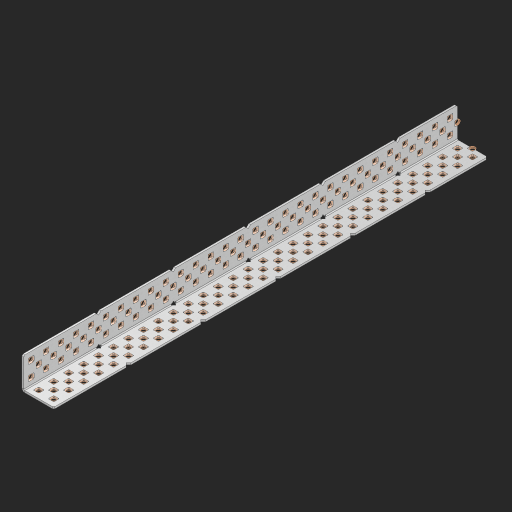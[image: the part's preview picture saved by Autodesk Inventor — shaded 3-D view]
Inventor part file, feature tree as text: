
AUTODESK INVENTOR PART (.ipt)
format: ipt  version: 2023 (Build 270158000, 158)  size: 2,022,912 bytes
history: native  units: in
note: dims shown in document units (in); Inventor stores cm internally (conversion verified against a paired STEP export)
features: other x180, extrude x172, sheet_metal_op x8, sketch x7, pattern_linear x2, mirror x1, chamfer x1
ambient origin geometry x8: Origin, YZ Plane, XZ Plane, XY Plane, X Axis, Y Axis, Z Axis, Center Point
bodies: Solid1 (feature_tree), Body (feature_tree)
feature tree (371):
  sheet_metal_op  "Flanges"
  sheet_metal_op  "Body Pattern"
  pattern_linear  "Center Pattern"  Spacing1=1.0in  [1 undecoded]
  other  "Arc Length"
  pattern_linear  "Notch Pattern"  Spacing1=0.25in  [1 undecoded]
  other  "Diagonal Plane"
  mirror  "Everything Mirrored"
  chamfer  "End Chamfer"
  sketch  "Sketch1"  dims[d0=1.0in]
  other  "Plate1"
  sketch  "Sketch2"  dims[d1=14.5in]
  other  "Plate2"
  sheet_metal_op  "Bend1"
  sheet_metal_op  "Corner1"
  sketch  "Sketch8"  dims[d2=0.0625in]
  sketch  "Sketch9"  dims[d3=0.0625in]
  other  "Srf91"
  sheet_metal_op  "Body Pattern Sketch"
  other  "Srf92"
  sketch  "Sketch13"  dims[d4=0.0312in]
  sketch  "Sketch15"  dims[d5=0.125in]
  sketch  "Sketch16"  dims[d6=0.0625in d7=1.0in d8=90.0deg d9=0.0312in d10=0.25in d11=0.0625in d12=0.0625in d49=0.182in d50=0.02in d52=0.25in d53=0.0625in d54=0.0in d55=0.172in d56=1.0in d57=0.0in d60=11.4173in d62=0.5in d63=0.7874in d65=0.5in d85=0.1473in d86=0.1782in d89=0.0625in d90=0.0in d91=0.04in d92=0.0491in d95=2.5in d96=0.04in d97=0.25in d98=45.0deg d99=0.25in d106=0.182in d107=0.02in d108=0.5in d110=0.0625in d111=0.0in d112=0.172in d113=0.5in d114=0.0in d117=0.5in d123=0.25in d125=0.25in d126=0.0491in d127=0.1473in d128=0.08in d129=0.04in d130=2.5in]
  other  "Srf786"
  other  "Srf856"
  other  "Srf857"
  other  "Srf858"
  other  "Srf859"
  other  "Srf860"
  other  "Srf861"
  other  "Srf889"
  other  "Srf890"
  other  "Srf891"
  other  "Srf1275"
  other  "Srf1276"
  other  "Srf1278"
  other  "Srf1279"
  other  "Srf1280"
  other  "Srf1281"
  other  "Srf1282"
  other  "Srf1283"
  other  "Srf1277"
  other  "Srf1285"
  other  "Srf1286"
  other  "Srf1287"
  other  "Srf1383"
  other  "Srf1384"
  other  "Srf1385"
  other  "Srf1386"
  other  "Srf1387"
  other  "Srf1388"
  other  "Srf1389"
  other  "Srf1390"
  other  "Srf1391"
  other  "Srf1392"
  other  "Srf1393"
  other  "Srf1394"
  other  "Srf1395"
  other  "Srf1396"
  other  "Srf1397"
  other  "Srf1398"
  other  "Srf1399"
  other  "Srf1400"
  other  "Srf1401"
  other  "Srf1402"
  other  "Srf1403"
  other  "Srf1404"
  other  "Srf1405"
  other  "Srf1406"
  other  "Srf1407"
  other  "Srf1408"
  other  "Srf1409"
  other  "Srf1410"
  other  "Srf1411"
  other  "Srf1412"
  other  "Srf1413"
  other  "Srf1414"
  other  "Srf1415"
  other  "Srf1416"
  other  "Srf1417"
  other  "Srf1418"
  other  "Srf1419"
  other  "Srf1420"
  other  "Srf1421"
  other  "Srf1422"
  other  "Srf1423"
  other  "Srf1424"
  other  "Srf1425"
  other  "Srf1426"
  other  "Srf1427"
  other  "Srf1428"
  other  "Srf1429"
  other  "Srf1430"
  other  "Srf1431"
  other  "Srf1432"
  other  "Srf1445"
  other  "Srf1446"
  other  "Srf1447"
  other  "Srf1448"
  other  "Srf1449"
  other  "Srf1450"
  other  "Srf1451"
  other  "Srf1452"
  other  "Srf1453"
  other  "Srf1454"
  other  "Srf1455"
  other  "Srf1456"
  other  "Srf1457"
  other  "Srf1458"
  other  "Srf1459"
  other  "Srf1460"
  other  "Srf1461"
  other  "Srf1462"
  other  "Srf1463"
  other  "Srf1464"
  other  "Srf1465"
  other  "Srf1466"
  other  "Srf1467"
  other  "Srf1468"
  other  "Srf1469"
  other  "Srf1475"
  other  "Srf1476"
  other  "Srf1477"
  other  "Srf1478"
  other  "Srf1479"
  other  "Srf1480"
  other  "Srf1481"
  other  "Srf1482"
  other  "Srf1483"
  other  "Srf1484"
  other  "Srf1485"
  other  "Srf1486"
  other  "Srf1487"
  other  "Srf1488"
  other  "Srf1489"
  other  "Srf1490"
  other  "Srf1491"
  other  "Srf1492"
  other  "Srf1493"
  other  "Srf1494"
  other  "Srf1495"
  other  "Srf1496"
  other  "Srf1497"
  other  "Srf1498"
  other  "Srf1499"
  other  "Srf1500"
  other  "Srf1501"
  other  "Srf1502"
  other  "Srf1503"
  other  "Srf1504"
  other  "Srf1505"
  other  "Srf1506"
  other  "Srf1507"
  other  "Srf1508"
  other  "Srf1509"
  other  "Srf1510"
  other  "Srf1511"
  other  "Srf1512"
  other  "Srf1513"
  other  "Srf1514"
  other  "Srf1515"
  other  "Srf1516"
  other  "Srf1517"
  other  "Srf1518"
  other  "Srf1519"
  other  "Srf1520"
  other  "Srf1521"
  other  "Srf1522"
  other  "Srf1523"
  other  "Srf1524"
  other  "Srf1537"
  other  "Srf1538"
  other  "Srf1539"
  other  "Srf1540"
  other  "Srf1541"
  other  "Srf1542"
  other  "Srf1543"
  other  "Srf1544"
  other  "Srf1545"
  other  "Srf1546"
  other  "Srf1547"
  other  "Srf1548"
  other  "Srf1549"
  other  "Srf1550"
  other  "Srf1551"
  other  "Srf1552"
  other  "Srf1553"
  other  "Srf1554"
  other  "Srf1555"
  other  "Srf1556"
  other  "Srf1557"
  other  "Srf1558"
  other  "Srf1559"
  other  "Srf1560"
  other  "Srf1561"
  sheet_metal_op  "Body Stamp"
  sheet_metal_op  "Body Circle"
  other  "Center Stamp"
  other  "Center Circle"
  sheet_metal_op  "Notch"
  extrude  "ExtrusionSrf92"  Depth=0.0625in
  extrude  "ExtrusionSrf856"  Depth=0.0625in
  extrude  "ExtrusionSrf857"  Depth=0.182in
  extrude  "ExtrusionSrf858"  Depth=0.02in
  extrude  "ExtrusionSrf859"  Depth=0.25in
  extrude  "ExtrusionSrf860"  Depth=0.0625in
  extrude  "ExtrusionSrf861"  TaperAngle=0.0deg  [1 undecoded]
  extrude  "ExtrusionSrf889"  Depth=2.5in
  extrude  "ExtrusionSrf890"  Depth=1.0in TaperAngle=0.0deg
  extrude  "ExtrusionSrf891"  Depth=2.5in
  extrude  "ExtrusionSrf1275"  Depth=0.5in
  extrude  "ExtrusionSrf1276"  Depth=2.5in
  extrude  "ExtrusionSrf1277"  Depth=2.5in
  extrude  "ExtrusionSrf1278"  Depth=0.0625in
  extrude  "ExtrusionSrf1279"  Depth=2.5in TaperAngle=0.0deg
  extrude  "ExtrusionSrf1280"  Depth=2.5in
  extrude  "ExtrusionSrf1281"  Depth=0.25in TaperAngle=45.0deg
  extrude  "ExtrusionSrf1282"  Depth=0.25in
  extrude  "ExtrusionSrf1345"  Depth=0.182in
  extrude  "ExtrusionSrf1346"  Depth=0.02in
  extrude  "ExtrusionSrf1347"  Depth=0.5in
  extrude  "ExtrusionSrf1348"  Depth=0.0625in
  extrude  "ExtrusionSrf1383"  TaperAngle=0.0deg  [1 undecoded]
  extrude  "ExtrusionSrf1384"  Depth=2.5in
  extrude  "ExtrusionSrf1385"  Depth=0.5in TaperAngle=0.0deg
  extrude  "ExtrusionSrf1386"  Depth=0.5in
  extrude  "ExtrusionSrf1387"  Depth=0.25in
  extrude  "ExtrusionSrf1388"  Depth=0.25in
  extrude  "ExtrusionSrf1389"  Depth=2.5in
  extrude  "ExtrusionSrf1390"  Depth=2.5in
  extrude  "ExtrusionSrf1391"  Depth=2.5in
  extrude  "ExtrusionSrf1392"  Depth=2.5in
  extrude  "ExtrusionSrf1393"  Depth=2.5in
  extrude  "ExtrusionSrf1394"  [1 undecoded]
  extrude  "ExtrusionSrf1395"  [1 undecoded]
  extrude  "ExtrusionSrf1396"  [1 undecoded]
  extrude  "ExtrusionSrf1397"  [1 undecoded]
  extrude  "ExtrusionSrf1398"  [1 undecoded]
  extrude  "ExtrusionSrf1399"  [1 undecoded]
  extrude  "ExtrusionSrf1400"  [1 undecoded]
  extrude  "ExtrusionSrf1401"  [1 undecoded]
  extrude  "ExtrusionSrf1402"  [1 undecoded]
  extrude  "ExtrusionSrf1403"  [1 undecoded]
  extrude  "ExtrusionSrf1404"  [1 undecoded]
  extrude  "ExtrusionSrf1405"  [1 undecoded]
  extrude  "ExtrusionSrf1406"  [1 undecoded]
  extrude  "ExtrusionSrf1407"  [1 undecoded]
  extrude  "ExtrusionSrf1408"  [1 undecoded]
  extrude  "ExtrusionSrf1409"  [1 undecoded]
  extrude  "ExtrusionSrf1410"  [1 undecoded]
  extrude  "ExtrusionSrf1411"  [1 undecoded]
  extrude  "ExtrusionSrf1412"  [1 undecoded]
  extrude  "ExtrusionSrf1413"  [1 undecoded]
  extrude  "ExtrusionSrf1414"  [1 undecoded]
  extrude  "ExtrusionSrf1415"  [1 undecoded]
  extrude  "ExtrusionSrf1416"  [1 undecoded]
  extrude  "ExtrusionSrf1417"  [1 undecoded]
  extrude  "ExtrusionSrf1418"  [1 undecoded]
  extrude  "ExtrusionSrf1419"  [1 undecoded]
  extrude  "ExtrusionSrf1420"  [1 undecoded]
  extrude  "ExtrusionSrf1421"  [1 undecoded]
  extrude  "ExtrusionSrf1422"  [1 undecoded]
  extrude  "ExtrusionSrf1423"  [1 undecoded]
  extrude  "ExtrusionSrf1424"  [1 undecoded]
  extrude  "ExtrusionSrf1425"  [1 undecoded]
  extrude  "ExtrusionSrf1426"  [1 undecoded]
  extrude  "ExtrusionSrf1427"  [1 undecoded]
  extrude  "ExtrusionSrf1428"  [1 undecoded]
  extrude  "ExtrusionSrf1429"  [1 undecoded]
  extrude  "ExtrusionSrf1430"  [1 undecoded]
  extrude  "ExtrusionSrf1431"  [1 undecoded]
  extrude  "ExtrusionSrf1432"  [1 undecoded]
  extrude  "ExtrusionSrf1445"  [1 undecoded]
  extrude  "ExtrusionSrf1446"  [1 undecoded]
  extrude  "ExtrusionSrf1447"  [1 undecoded]
  extrude  "ExtrusionSrf1448"  [1 undecoded]
  extrude  "ExtrusionSrf1449"  [1 undecoded]
  extrude  "ExtrusionSrf1450"  [1 undecoded]
  extrude  "ExtrusionSrf1451"  [1 undecoded]
  extrude  "ExtrusionSrf1452"  [1 undecoded]
  extrude  "ExtrusionSrf1453"  [1 undecoded]
  extrude  "ExtrusionSrf1454"  [1 undecoded]
  extrude  "ExtrusionSrf1455"  [1 undecoded]
  extrude  "ExtrusionSrf1456"  [1 undecoded]
  extrude  "ExtrusionSrf1457"  [1 undecoded]
  extrude  "ExtrusionSrf1458"  [1 undecoded]
  extrude  "ExtrusionSrf1459"  [1 undecoded]
  extrude  "ExtrusionSrf1460"  [1 undecoded]
  extrude  "ExtrusionSrf1461"  [1 undecoded]
  extrude  "ExtrusionSrf1462"  [1 undecoded]
  extrude  "ExtrusionSrf1463"  [1 undecoded]
  extrude  "ExtrusionSrf1464"  [1 undecoded]
  extrude  "ExtrusionSrf1465"  [1 undecoded]
  extrude  "ExtrusionSrf1466"  [1 undecoded]
  extrude  "ExtrusionSrf1467"  [1 undecoded]
  extrude  "ExtrusionSrf1468"  [1 undecoded]
  extrude  "ExtrusionSrf1469"  [1 undecoded]
  extrude  "ExtrusionSrf1475"  [1 undecoded]
  extrude  "ExtrusionSrf1476"  [1 undecoded]
  extrude  "ExtrusionSrf1477"  [1 undecoded]
  extrude  "ExtrusionSrf1478"  [1 undecoded]
  extrude  "ExtrusionSrf1479"  [1 undecoded]
  extrude  "ExtrusionSrf1480"  [1 undecoded]
  extrude  "ExtrusionSrf1481"  [1 undecoded]
  extrude  "ExtrusionSrf1482"  [1 undecoded]
  extrude  "ExtrusionSrf1483"  [1 undecoded]
  extrude  "ExtrusionSrf1484"  [1 undecoded]
  extrude  "ExtrusionSrf1485"  [1 undecoded]
  extrude  "ExtrusionSrf1486"  [1 undecoded]
  extrude  "ExtrusionSrf1487"  [1 undecoded]
  extrude  "ExtrusionSrf1488"  [1 undecoded]
  extrude  "ExtrusionSrf1489"  [1 undecoded]
  extrude  "ExtrusionSrf1490"  [1 undecoded]
  extrude  "ExtrusionSrf1491"  [1 undecoded]
  extrude  "ExtrusionSrf1492"  [1 undecoded]
  extrude  "ExtrusionSrf1493"  [1 undecoded]
  extrude  "ExtrusionSrf1494"  [1 undecoded]
  extrude  "ExtrusionSrf1495"  [1 undecoded]
  extrude  "ExtrusionSrf1496"  [1 undecoded]
  extrude  "ExtrusionSrf1497"  [1 undecoded]
  extrude  "ExtrusionSrf1498"  [1 undecoded]
  extrude  "ExtrusionSrf1499"  [1 undecoded]
  extrude  "ExtrusionSrf1500"  [1 undecoded]
  extrude  "ExtrusionSrf1501"  [1 undecoded]
  extrude  "ExtrusionSrf1502"  [1 undecoded]
  extrude  "ExtrusionSrf1503"  [1 undecoded]
  extrude  "ExtrusionSrf1504"  [1 undecoded]
  extrude  "ExtrusionSrf1505"  [1 undecoded]
  extrude  "ExtrusionSrf1506"  [1 undecoded]
  extrude  "ExtrusionSrf1507"  [1 undecoded]
  extrude  "ExtrusionSrf1508"  [1 undecoded]
  extrude  "ExtrusionSrf1509"  [1 undecoded]
  extrude  "ExtrusionSrf1510"  [1 undecoded]
  extrude  "ExtrusionSrf1511"  [1 undecoded]
  extrude  "ExtrusionSrf1512"  [1 undecoded]
  extrude  "ExtrusionSrf1513"  [1 undecoded]
  extrude  "ExtrusionSrf1514"  [1 undecoded]
  extrude  "ExtrusionSrf1515"  [1 undecoded]
  extrude  "ExtrusionSrf1516"  [1 undecoded]
  extrude  "ExtrusionSrf1517"  [1 undecoded]
  extrude  "ExtrusionSrf1518"  [1 undecoded]
  extrude  "ExtrusionSrf1519"  [1 undecoded]
  extrude  "ExtrusionSrf1520"  [1 undecoded]
  extrude  "ExtrusionSrf1521"  [1 undecoded]
  extrude  "ExtrusionSrf1522"  [1 undecoded]
  extrude  "ExtrusionSrf1523"  [1 undecoded]
  extrude  "ExtrusionSrf1524"  [1 undecoded]
  extrude  "ExtrusionSrf1537"  [1 undecoded]
  extrude  "ExtrusionSrf1538"  [1 undecoded]
  extrude  "ExtrusionSrf1539"  [1 undecoded]
  extrude  "ExtrusionSrf1540"  [1 undecoded]
  extrude  "ExtrusionSrf1541"  [1 undecoded]
  extrude  "ExtrusionSrf1542"  [1 undecoded]
  extrude  "ExtrusionSrf1543"  [1 undecoded]
  extrude  "ExtrusionSrf1544"  [1 undecoded]
  extrude  "ExtrusionSrf1545"  [1 undecoded]
  extrude  "ExtrusionSrf1546"  [1 undecoded]
  extrude  "ExtrusionSrf1547"  [1 undecoded]
  extrude  "ExtrusionSrf1548"  [1 undecoded]
  extrude  "ExtrusionSrf1549"  [1 undecoded]
  extrude  "ExtrusionSrf1550"  [1 undecoded]
  extrude  "ExtrusionSrf1551"  [1 undecoded]
  extrude  "ExtrusionSrf1552"  [1 undecoded]
  extrude  "ExtrusionSrf1553"  [1 undecoded]
  extrude  "ExtrusionSrf1554"  [1 undecoded]
  extrude  "ExtrusionSrf1555"  [1 undecoded]
  extrude  "ExtrusionSrf1556"  [1 undecoded]
  extrude  "ExtrusionSrf1557"  [1 undecoded]
  extrude  "ExtrusionSrf1558"  [1 undecoded]
  extrude  "ExtrusionSrf1559"  [1 undecoded]
  extrude  "ExtrusionSrf1560"  [1 undecoded]
  extrude  "ExtrusionSrf1561"  [1 undecoded]
note: 143 required parameter values undecoded (feature->parameter linkage not recoverable at this tier; creation-order binding heuristic only, values carry confidence <= 0.55)
